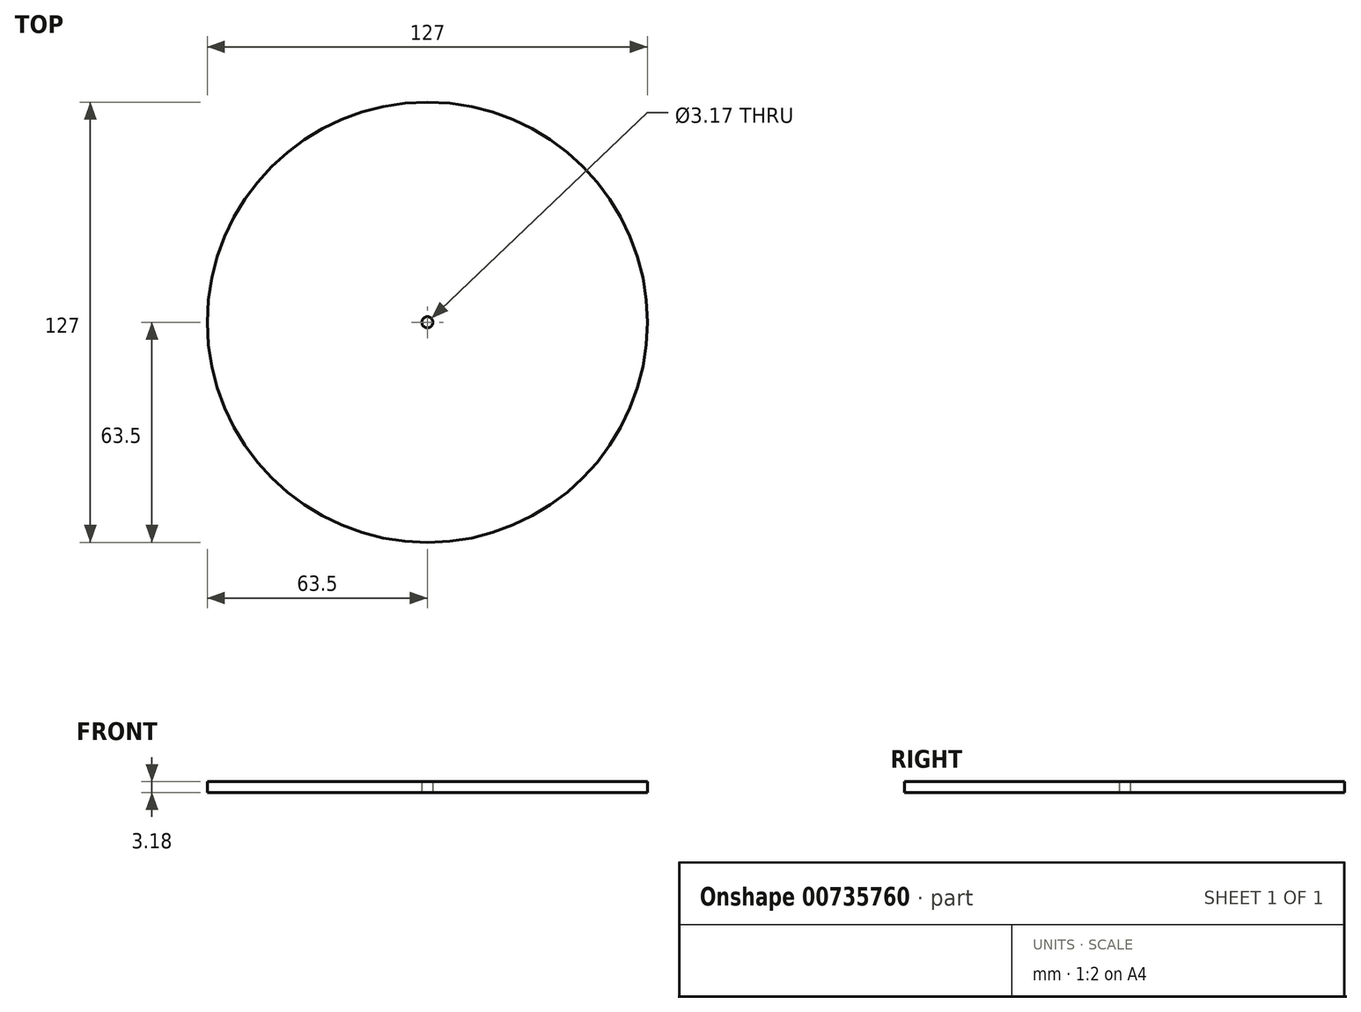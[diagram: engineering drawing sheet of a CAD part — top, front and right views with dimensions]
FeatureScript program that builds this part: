
annotation { "Feature Type Name" : "Feature", "Feature Type Description" : "" }
export const myFeature = defineFeature(function(context is Context, id is Id, definition is map)
    precondition{}
    {
        {
            var Q0;
            Q0=qCreatedBy(makeId("Top.planeOp"),FACE);
            var sketch = newSketch(context, id + "F0", { "sketchPlane" : qUnion([Q0])});
            skCircle(sketch, "E0", {"center": v(0, 0) * mm, "radius": 63.5 * mm});
            skCircle(sketch, "E1", {"center": v(0, 0) * mm, "radius": 1.59 * mm});
            skSolve(sketch);
        }
        {
            var Q0;
            Q0=makeQuery(id+"F0.imprint","IMPRINT",FACE,{"disambiguationData":[TD([[makeQuery(id+"F0.imprint","IMPRINT",EDGE,{"derivedFrom":sQuery(id+"F0.wireOp",EDGE,"E0")}),1.0]])]});
            extrude(context, id + "F1", {"entities" : qUnion([Q0]), "depth" : 3.17 * mm, "offsetDistance" : 25.4 * mm});
        }
    });
